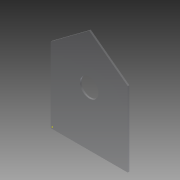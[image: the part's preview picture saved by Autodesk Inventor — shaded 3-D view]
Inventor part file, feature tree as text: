
AUTODESK INVENTOR PART (.ipt)
format: ipt  version: 2015 (Build 190159000, 159)  size: 115,712 bytes
history: native  units: in
note: dims shown in document units (in); Inventor stores cm internally (conversion verified against a paired STEP export)
features: sketch x5, extrude x4
ambient origin geometry x8: Origin, YZ Plane, XZ Plane, XY Plane, X Axis, Y Axis, Z Axis, Center Point
bodies: Solid1 (feature_tree)
feature tree (9):
  sketch  "Sketch1"  dims[d0=13.189in d1=17.7165in]
  extrude  "Extrusion1"  Depth=17.7165in
  extrude  "Extrusion2"  Depth=0.2756in TaperAngle=0.0deg
  extrude  "Extrusion3"  Depth=12.7953in
  extrude  "Extrusion6"  Depth=12.7953in
  sketch  "Sketch2"  dims[d2=6.5945in d3=0.2756in d4=0.0in]
  sketch  "Sketch3"  dims[d5=6.5945in d6=12.7953in]
  sketch  "Sketch5"  dims[d7=6.5369in d8=0.0in d10=12.7953in]
  sketch  "Sketch11"  dims[d11=12.0256in d12=0.0in d29=1.9291in d30=3.189in d31=0.3937in d32=0.0in]
